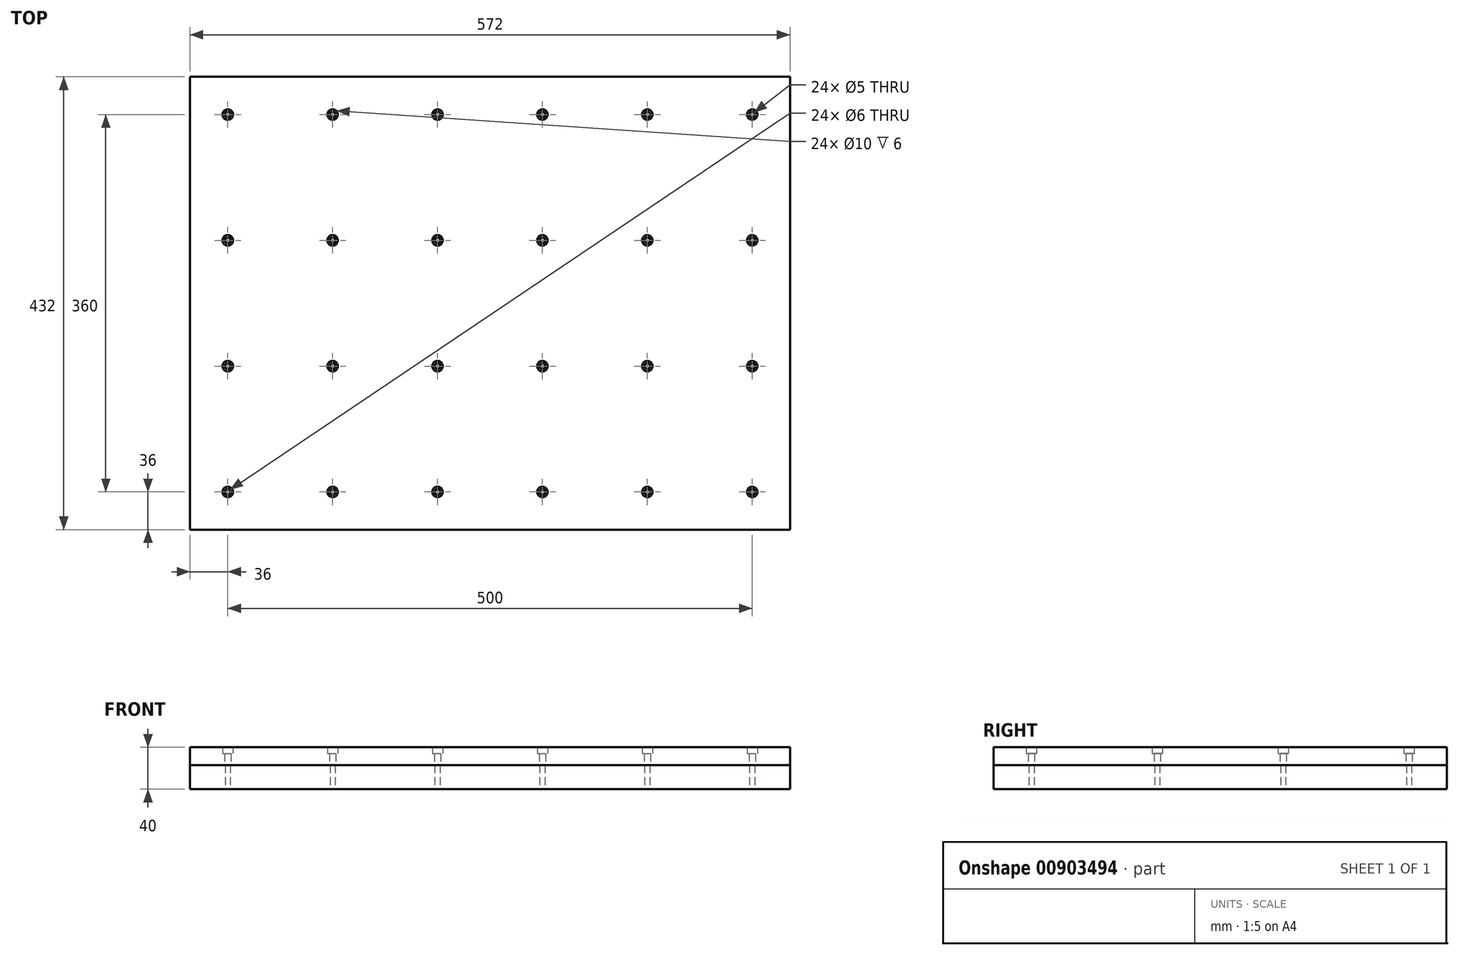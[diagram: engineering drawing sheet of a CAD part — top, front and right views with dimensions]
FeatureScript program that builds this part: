
annotation { "Feature Type Name" : "Feature", "Feature Type Description" : "" }
export const myFeature = defineFeature(function(context is Context, id is Id, definition is map)
    precondition{}
    {
        {
            var Q0;
            Q0=qCreatedBy(makeId("Top.planeOp"),FACE);
            var sketch = newSketch(context, id + "F0", { "sketchPlane" : qUnion([Q0])});
            skLineSegment(sketch, "E0.bottom", {"start": v(0, 0) * mm, "end": v(100, 0) * mm, "construction": true});
            skLineSegment(sketch, "E0.top", {"start": v(0, 120) * mm, "end": v(100, 120) * mm, "construction": true});
            skLineSegment(sketch, "E0.left", {"start": v(0, 0) * mm, "end": v(0, 120) * mm, "construction": true});
            skLineSegment(sketch, "E0.right", {"start": v(100, 0) * mm, "end": v(100, 120) * mm, "construction": true});
            skLineSegment(sketch, "E1.0.1.0", {"start": v(100, 120) * mm, "end": v(100, 240) * mm, "construction": true});
            skLineSegment(sketch, "E1.0.1.1", {"start": v(0, 240) * mm, "end": v(100, 240) * mm, "construction": true});
            skLineSegment(sketch, "E1.0.1.2", {"start": v(0, 120) * mm, "end": v(0, 240) * mm, "construction": true});
            skLineSegment(sketch, "E1.0.2.0", {"start": v(100, 240) * mm, "end": v(100, 360) * mm, "construction": true});
            skLineSegment(sketch, "E1.0.2.1", {"start": v(0, 360) * mm, "end": v(100, 360) * mm, "construction": true});
            skLineSegment(sketch, "E1.0.2.2", {"start": v(0, 240) * mm, "end": v(0, 360) * mm, "construction": true});
            skLineSegment(sketch, "E1.0.2.3", {"start": v(0, 240) * mm, "end": v(100, 240) * mm, "construction": true});
            skLineSegment(sketch, "E1.1.0.0", {"start": v(200, 0) * mm, "end": v(200, 120) * mm, "construction": true});
            skLineSegment(sketch, "E1.1.0.1", {"start": v(100, 120) * mm, "end": v(200, 120) * mm, "construction": true});
            skLineSegment(sketch, "E1.1.0.3", {"start": v(100, 0) * mm, "end": v(200, 0) * mm, "construction": true});
            skLineSegment(sketch, "E1.1.1.0", {"start": v(200, 120) * mm, "end": v(200, 240) * mm, "construction": true});
            skLineSegment(sketch, "E1.1.1.1", {"start": v(100, 240) * mm, "end": v(200, 240) * mm, "construction": true});
            skLineSegment(sketch, "E1.1.1.2", {"start": v(100, 120) * mm, "end": v(100, 240) * mm, "construction": true});
            skLineSegment(sketch, "E1.1.1.3", {"start": v(100, 120) * mm, "end": v(200, 120) * mm, "construction": true});
            skLineSegment(sketch, "E1.1.2.0", {"start": v(200, 240) * mm, "end": v(200, 360) * mm, "construction": true});
            skLineSegment(sketch, "E1.1.2.1", {"start": v(100, 360) * mm, "end": v(200, 360) * mm, "construction": true});
            skLineSegment(sketch, "E1.1.2.2", {"start": v(100, 240) * mm, "end": v(100, 360) * mm, "construction": true});
            skLineSegment(sketch, "E1.1.2.3", {"start": v(100, 240) * mm, "end": v(200, 240) * mm, "construction": true});
            skLineSegment(sketch, "E1.2.0.0", {"start": v(300, 0) * mm, "end": v(300, 120) * mm, "construction": true});
            skLineSegment(sketch, "E1.2.0.1", {"start": v(200, 120) * mm, "end": v(300, 120) * mm, "construction": true});
            skLineSegment(sketch, "E1.2.0.2", {"start": v(200, 0) * mm, "end": v(200, 120) * mm, "construction": true});
            skLineSegment(sketch, "E1.2.0.3", {"start": v(200, 0) * mm, "end": v(300, 0) * mm, "construction": true});
            skLineSegment(sketch, "E1.2.1.0", {"start": v(300, 120) * mm, "end": v(300, 240) * mm, "construction": true});
            skLineSegment(sketch, "E1.2.1.1", {"start": v(200, 240) * mm, "end": v(300, 240) * mm, "construction": true});
            skLineSegment(sketch, "E1.2.1.2", {"start": v(200, 120) * mm, "end": v(200, 240) * mm, "construction": true});
            skLineSegment(sketch, "E1.2.1.3", {"start": v(200, 120) * mm, "end": v(300, 120) * mm, "construction": true});
            skLineSegment(sketch, "E1.2.2.0", {"start": v(300, 240) * mm, "end": v(300, 360) * mm, "construction": true});
            skLineSegment(sketch, "E1.2.2.1", {"start": v(200, 360) * mm, "end": v(300, 360) * mm, "construction": true});
            skLineSegment(sketch, "E1.2.2.2", {"start": v(200, 240) * mm, "end": v(200, 360) * mm, "construction": true});
            skLineSegment(sketch, "E1.2.2.3", {"start": v(200, 240) * mm, "end": v(300, 240) * mm, "construction": true});
            skLineSegment(sketch, "E1.3.0.0", {"start": v(400, 0) * mm, "end": v(400, 120) * mm, "construction": true});
            skLineSegment(sketch, "E1.3.0.1", {"start": v(300, 120) * mm, "end": v(400, 120) * mm, "construction": true});
            skLineSegment(sketch, "E1.3.0.2", {"start": v(300, 0) * mm, "end": v(300, 120) * mm, "construction": true});
            skLineSegment(sketch, "E1.3.0.3", {"start": v(300, 0) * mm, "end": v(400, 0) * mm, "construction": true});
            skLineSegment(sketch, "E1.3.1.0", {"start": v(400, 120) * mm, "end": v(400, 240) * mm, "construction": true});
            skLineSegment(sketch, "E1.3.1.1", {"start": v(300, 240) * mm, "end": v(400, 240) * mm, "construction": true});
            skLineSegment(sketch, "E1.3.1.2", {"start": v(300, 120) * mm, "end": v(300, 240) * mm, "construction": true});
            skLineSegment(sketch, "E1.3.1.3", {"start": v(300, 120) * mm, "end": v(400, 120) * mm, "construction": true});
            skLineSegment(sketch, "E1.3.2.0", {"start": v(400, 240) * mm, "end": v(400, 360) * mm, "construction": true});
            skLineSegment(sketch, "E1.3.2.1", {"start": v(300, 360) * mm, "end": v(400, 360) * mm, "construction": true});
            skLineSegment(sketch, "E1.3.2.2", {"start": v(300, 240) * mm, "end": v(300, 360) * mm, "construction": true});
            skLineSegment(sketch, "E1.3.2.3", {"start": v(300, 240) * mm, "end": v(400, 240) * mm, "construction": true});
            skLineSegment(sketch, "E1.4.0.0", {"start": v(500, 0) * mm, "end": v(500, 120) * mm, "construction": true});
            skLineSegment(sketch, "E1.4.0.1", {"start": v(400, 120) * mm, "end": v(500, 120) * mm, "construction": true});
            skLineSegment(sketch, "E1.4.0.2", {"start": v(400, 0) * mm, "end": v(400, 120) * mm, "construction": true});
            skLineSegment(sketch, "E1.4.0.3", {"start": v(400, 0) * mm, "end": v(500, 0) * mm, "construction": true});
            skLineSegment(sketch, "E1.4.1.0", {"start": v(500, 120) * mm, "end": v(500, 240) * mm, "construction": true});
            skLineSegment(sketch, "E1.4.1.1", {"start": v(400, 240) * mm, "end": v(500, 240) * mm, "construction": true});
            skLineSegment(sketch, "E1.4.1.2", {"start": v(400, 120) * mm, "end": v(400, 240) * mm, "construction": true});
            skLineSegment(sketch, "E1.4.1.3", {"start": v(400, 120) * mm, "end": v(500, 120) * mm, "construction": true});
            skLineSegment(sketch, "E1.4.2.0", {"start": v(500, 240) * mm, "end": v(500, 360) * mm, "construction": true});
            skLineSegment(sketch, "E1.4.2.1", {"start": v(400, 360) * mm, "end": v(500, 360) * mm, "construction": true});
            skLineSegment(sketch, "E1.4.2.2", {"start": v(400, 240) * mm, "end": v(400, 360) * mm, "construction": true});
            skLineSegment(sketch, "E1.4.2.3", {"start": v(400, 240) * mm, "end": v(500, 240) * mm, "construction": true});
            skSolve(sketch);
        }
        {
            var Q0;
            Q0=qCreatedBy(makeId("Top.planeOp"),FACE);
            var sketch = newSketch(context, id + "F1", { "sketchPlane" : qUnion([Q0])});
            skPoint(sketch, "E2.0", {"position": v(0, 360) * mm});
            skPoint(sketch, "E3.0", {"position": v(500, 360) * mm});
            skPoint(sketch, "E4.0", {"position": v(500, 0) * mm});
            skPoint(sketch, "E5.0", {"position": v(0, 0) * mm});
            skLineSegment(sketch, "E6.bottom", {"start": v(0, 0) * mm, "end": v(500, 0) * mm});
            skLineSegment(sketch, "E6.top", {"start": v(0, 360) * mm, "end": v(500, 360) * mm});
            skLineSegment(sketch, "E6.left", {"start": v(0, 0) * mm, "end": v(0, 360) * mm});
            skLineSegment(sketch, "E6.right", {"start": v(500, 0) * mm, "end": v(500, 360) * mm});
            skLineSegment(sketch, "E7.0", {"start": v(536, -36) * mm, "end": v(536, 396) * mm});
            skLineSegment(sketch, "E7.1", {"start": v(-36, -36) * mm, "end": v(536, -36) * mm});
            skLineSegment(sketch, "E7.2", {"start": v(-36, -36) * mm, "end": v(-36, 396) * mm});
            skLineSegment(sketch, "E7.3", {"start": v(-36, 396) * mm, "end": v(536, 396) * mm});
            skSolve(sketch);
        }
        {
            var Q0;
            Q0=makeQuery(id+"F1.imprint","IMPRINT",FACE,{"disambiguationData":[TD([[makeQuery(id+"F1.imprint","IMPRINT",EDGE,{"derivedFrom":sQuery(id+"F1.wireOp",EDGE,"E6.bottom")}),1.0]])]});
            var Q1;
            Q1=makeQuery(id+"F1.imprint","IMPRINT",FACE,{"disambiguationData":[TD([[makeQuery(id+"F1.imprint","IMPRINT",EDGE,{"derivedFrom":sQuery(id+"F1.wireOp",EDGE,"E6.bottom")}),-1.0]])]});
            extrude(context, id + "F2", {"entities" : qUnion([Q0, Q1]), "oppositeDirection" : true, "depth" : 40 * mm, "offsetDistance" : 25 * mm, "hasSecondDirection" : true, "secondDirectionOppositeDirection" : true, "secondDirectionDepth" : 17 * mm});
        }
        {
            var Q0;
            Q0=makeQuery(id+"F2.opExtrude","CAP_FACE",FACE,{"disambiguationData":[OSD([sQuery(id+"F1.wireOp",EDGE,"E7.0"),sQuery(id+"F1.wireOp",EDGE,"E7.1"),sQuery(id+"F1.wireOp",EDGE,"E7.2"),sQuery(id+"F1.wireOp",EDGE,"E7.3")])],"isStart":true});
            var Q1;
            Q1=qCreatedBy(makeId("Top.planeOp"),FACE);
            extrude(context, id + "F3", {"entities" : qUnion([Q0]), "endBound" : BoundingType.UP_TO_SURFACE, "depth" : 20 * mm, "endBoundEntityFace" : qUnion([Q1]), "offsetDistance" : 25 * mm});
        }
        {
            var Q0;
            Q0=sQuery(id+"F0.wireOp",VERTEX,"E1.0.2.1.end");
            var Q1;
            Q1=sQuery(id+"F0.wireOp",VERTEX,"E1.2.1.3.end");
            var Q2;
            Q2=sQuery(id+"F0.wireOp",VERTEX,"E1.4.0.0.start");
            var Q3;
            Q3=sQuery(id+"F0.wireOp",VERTEX,"E1.2.2.0.end");
            var Q4;
            Q4=sQuery(id+"F0.wireOp",VERTEX,"E0.right.end");
            var Q5;
            Q5=sQuery(id+"F0.wireOp",VERTEX,"E1.1.1.0.end");
            var Q6;
            Q6=sQuery(id+"F0.wireOp",VERTEX,"E1.4.2.0.end");
            var Q7;
            Q7=sQuery(id+"F0.wireOp",VERTEX,"E1.3.0.2.start");
            var Q8;
            Q8=sQuery(id+"F0.wireOp",VERTEX,"E1.4.0.2.start");
            var Q9;
            Q9=sQuery(id+"F0.wireOp",VERTEX,"E1.1.0.3.end");
            var Q10;
            Q10=sQuery(id+"F0.wireOp",VERTEX,"E1.4.1.0.end");
            var Q11;
            Q11=sQuery(id+"F0.wireOp",VERTEX,"E1.1.0.1.end");
            var Q12;
            Q12=sQuery(id+"F0.wireOp",VERTEX,"E1.2.2.1.start");
            var Q13;
            Q13=sQuery(id+"F0.wireOp",VERTEX,"E1.0.2.3.start");
            var Q14;
            Q14=sQuery(id+"F0.wireOp",VERTEX,"E0.right.start");
            var Q15;
            Q15=sQuery(id+"F0.wireOp",VERTEX,"E1.4.0.1.start");
            var Q16;
            Q16=sQuery(id+"F0.wireOp",VERTEX,"E1.0.2.3.end");
            var Q17;
            Q17=sQuery(id+"F0.wireOp",VERTEX,"E0.left.end");
            var Q18;
            Q18=sQuery(id+"F0.wireOp",VERTEX,"E1.4.0.0.end");
            var Q19;
            Q19=sQuery(id+"F0.wireOp",VERTEX,"E1.3.2.3.end");
            var Q20;
            Q20=sQuery(id+"F0.wireOp",VERTEX,"E1.2.2.0.start");
            var Q21;
            Q21=sQuery(id+"F0.wireOp",VERTEX,"E1.0.2.2.end");
            var Q22;
            Q22=sQuery(id+"F0.wireOp",VERTEX,"E0.left.start");
            var Q23;
            Q23=sQuery(id+"F0.wireOp",VERTEX,"E1.3.2.1.end");
            var Q24;
            Q24=makeQuery(id+"F2.opExtrude","SWEPT_BODY",BODY,{"disambiguationData":[OSD([sQuery(id+"F1.wireOp",EDGE,"E7.0"),sQuery(id+"F1.wireOp",EDGE,"E7.1"),sQuery(id+"F1.wireOp",EDGE,"E7.2"),sQuery(id+"F1.wireOp",EDGE,"E7.3")])]});
            hole(context, id + "F4", {"style" : HoleStyle.SIMPLE, "endStyle" : HoleEndStyle.THROUGH, "standardTappedOrClearance" : lookupTablePath({ "standard" : "ISO", "engagement" : "75%", "pitch" : "1 mm", "size" : "M6", "type" : "Tapped" }), "standardBlindInLast" : lookupTablePath({ "standard" : "ISO", "fit" : "Normal", "engagement" : "75%", "pitch" : "1 mm", "size" : "M6", "type" : "Clearance & tapped" }), "holeDiameter" : 5 * mm, "majorDiameter" : 6 * mm, "showTappedDepth" : true, "isTappedThrough" : true, "tappedDepth" : 12 * mm, "tapClearance" : 3, "locations" : qUnion([Q0, Q1, Q2, Q3, Q4, Q5, Q6, Q7, Q8, Q9, Q10, Q11, Q12, Q13, Q14, Q15, Q16, Q17, Q18, Q19, Q20, Q21, Q22, Q23]), "scope" : qUnion([Q24]), "startStyle" : HoleStartStyle.PART});
        }
        {
            var Q0;
            Q0=sQuery(id+"F0.wireOp",VERTEX,"E0.left.end");
            var Q1;
            Q1=sQuery(id+"F0.wireOp",VERTEX,"E1.0.2.3.start");
            var Q2;
            Q2=sQuery(id+"F0.wireOp",VERTEX,"E1.2.2.0.start");
            var Q3;
            Q3=sQuery(id+"F0.wireOp",VERTEX,"E1.0.2.1.end");
            var Q4;
            Q4=sQuery(id+"F0.wireOp",VERTEX,"E1.4.0.0.end");
            var Q5;
            Q5=sQuery(id+"F0.wireOp",VERTEX,"E1.4.0.1.start");
            var Q6;
            Q6=sQuery(id+"F0.wireOp",VERTEX,"E1.0.2.2.end");
            var Q7;
            Q7=sQuery(id+"F0.wireOp",VERTEX,"E1.3.2.3.end");
            var Q8;
            Q8=sQuery(id+"F0.wireOp",VERTEX,"E1.1.1.0.end");
            var Q9;
            Q9=sQuery(id+"F0.wireOp",VERTEX,"E1.4.0.0.start");
            var Q10;
            Q10=sQuery(id+"F0.wireOp",VERTEX,"E1.3.2.1.end");
            var Q11;
            Q11=sQuery(id+"F0.wireOp",VERTEX,"E0.right.end");
            var Q12;
            Q12=sQuery(id+"F0.wireOp",VERTEX,"E1.4.2.0.end");
            var Q13;
            Q13=sQuery(id+"F0.wireOp",VERTEX,"E1.0.2.3.end");
            var Q14;
            Q14=sQuery(id+"F0.wireOp",VERTEX,"E1.4.0.2.start");
            var Q15;
            Q15=sQuery(id+"F0.wireOp",VERTEX,"E1.2.2.0.end");
            var Q16;
            Q16=sQuery(id+"F0.wireOp",VERTEX,"E0.left.start");
            var Q17;
            Q17=sQuery(id+"F0.wireOp",VERTEX,"E1.1.0.3.end");
            var Q18;
            Q18=sQuery(id+"F0.wireOp",VERTEX,"E0.right.start");
            var Q19;
            Q19=sQuery(id+"F0.wireOp",VERTEX,"E1.2.1.3.end");
            var Q20;
            Q20=sQuery(id+"F0.wireOp",VERTEX,"E1.1.0.1.end");
            var Q21;
            Q21=sQuery(id+"F0.wireOp",VERTEX,"E1.3.0.2.start");
            var Q22;
            Q22=sQuery(id+"F0.wireOp",VERTEX,"E1.4.1.0.end");
            var Q23;
            Q23=sQuery(id+"F0.wireOp",VERTEX,"E1.2.2.1.start");
            var Q24;
            Q24=makeQuery(id+"F3.opExtrude","SWEPT_BODY",BODY,{"disambiguationData":[OSD([sQuery(id+"F1.wireOp",EDGE,"E7.0"),sQuery(id+"F1.wireOp",EDGE,"E7.1"),sQuery(id+"F1.wireOp",EDGE,"E7.2"),sQuery(id+"F1.wireOp",EDGE,"E7.3")])]});
            hole(context, id + "F5", {"style" : HoleStyle.C_BORE, "endStyle" : HoleEndStyle.THROUGH, "holeDiameter" : 6 * mm, "cBoreDiameter" : 10 * mm, "cBoreDepth" : 6 * mm, "majorDiameter" : 6 * mm, "isTappedThrough" : true, "tappedDepth" : 12 * mm, "tapClearance" : 3, "locations" : qUnion([Q0, Q1, Q2, Q3, Q4, Q5, Q6, Q7, Q8, Q9, Q10, Q11, Q12, Q13, Q14, Q15, Q16, Q17, Q18, Q19, Q20, Q21, Q22, Q23]), "scope" : qUnion([Q24]), "startStyle" : HoleStartStyle.PART});
        }
    });
